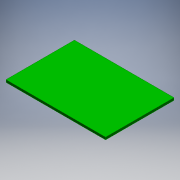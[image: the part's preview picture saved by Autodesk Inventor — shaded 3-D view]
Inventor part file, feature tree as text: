
AUTODESK INVENTOR PART (.ipt)
format: ipt  version: 2016 (Build 200138000, 138)  size: 109,056 bytes
history: native  units: mm
features: sketch x1, extrude x1
ambient origin geometry x8: Origin, YZ Plane, XZ Plane, XY Plane, X Axis, Y Axis, Z Axis, Center Point
bodies: Body1 (feature_tree)
feature tree (2):
  sketch  "スケッチ1"
  extrude  "押し出し5"  Depth=17.0mm
